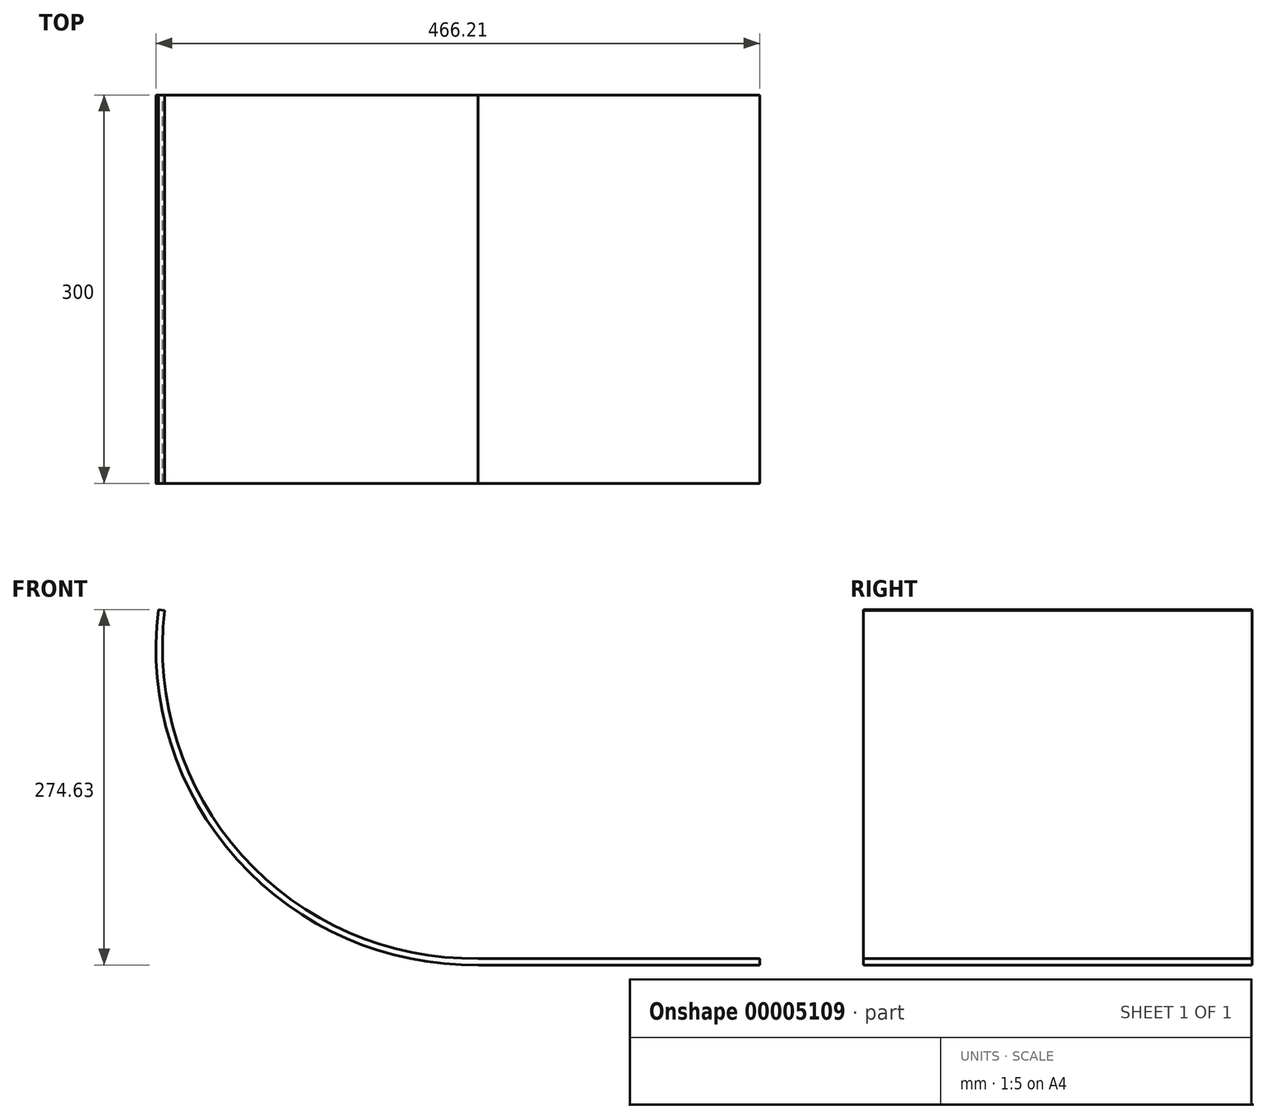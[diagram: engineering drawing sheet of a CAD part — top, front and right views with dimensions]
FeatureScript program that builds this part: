
annotation { "Feature Type Name" : "Feature", "Feature Type Description" : "" }
export const myFeature = defineFeature(function(context is Context, id is Id, definition is map)
    precondition{}
    {
        {
            var Q0;
            Q0=qCreatedBy(makeId("Front.planeOp"),FACE);
            var sketch = newSketch(context, id + "F0", { "sketchPlane" : qUnion([Q0])});
            skArc(sketch, "E0", {"start": v(-277, 158.39) * mm, "mid": v(-217.17, -31.17) * mm, "end": v(-34.97, -110.61) * mm});
            skLineSegment(sketch, "E1", {"start": v(-42.55, -110.61) * mm, "end": v(182.45, -110.61) * mm});
            skArc(sketch, "E2.0", {"start": v(-281.96, 158.99) * mm, "mid": v(-220.89, -34.51) * mm, "end": v(-34.9, -115.61) * mm});
            skLineSegment(sketch, "E3.0", {"start": v(-42.55, -115.61) * mm, "end": v(182.45, -115.61) * mm});
            skLineSegment(sketch, "E4", {"start": v(-281.96, 158.99) * mm, "end": v(-277, 158.39) * mm});
            skLineSegment(sketch, "E5", {"start": v(182.45, -110.61) * mm, "end": v(182.45, -115.61) * mm});
            skSolve(sketch);
        }
        {
            var Q0;
            {var subQ1=sQuery(id+"F0.wireOp",EDGE,"E4");Q0=makeQuery(id+"F0.imprint","IMPRINT",FACE,{"disambiguationData":[TD([[makeQuery(id+"F0.imprint","IMPRINT",EDGE,{"derivedFrom":subQ1}),-1.0]])]});}
            extrude(context, id + "F1", {"entities" : qUnion([Q0]), "depth" : 300 * mm});
        }
    });
